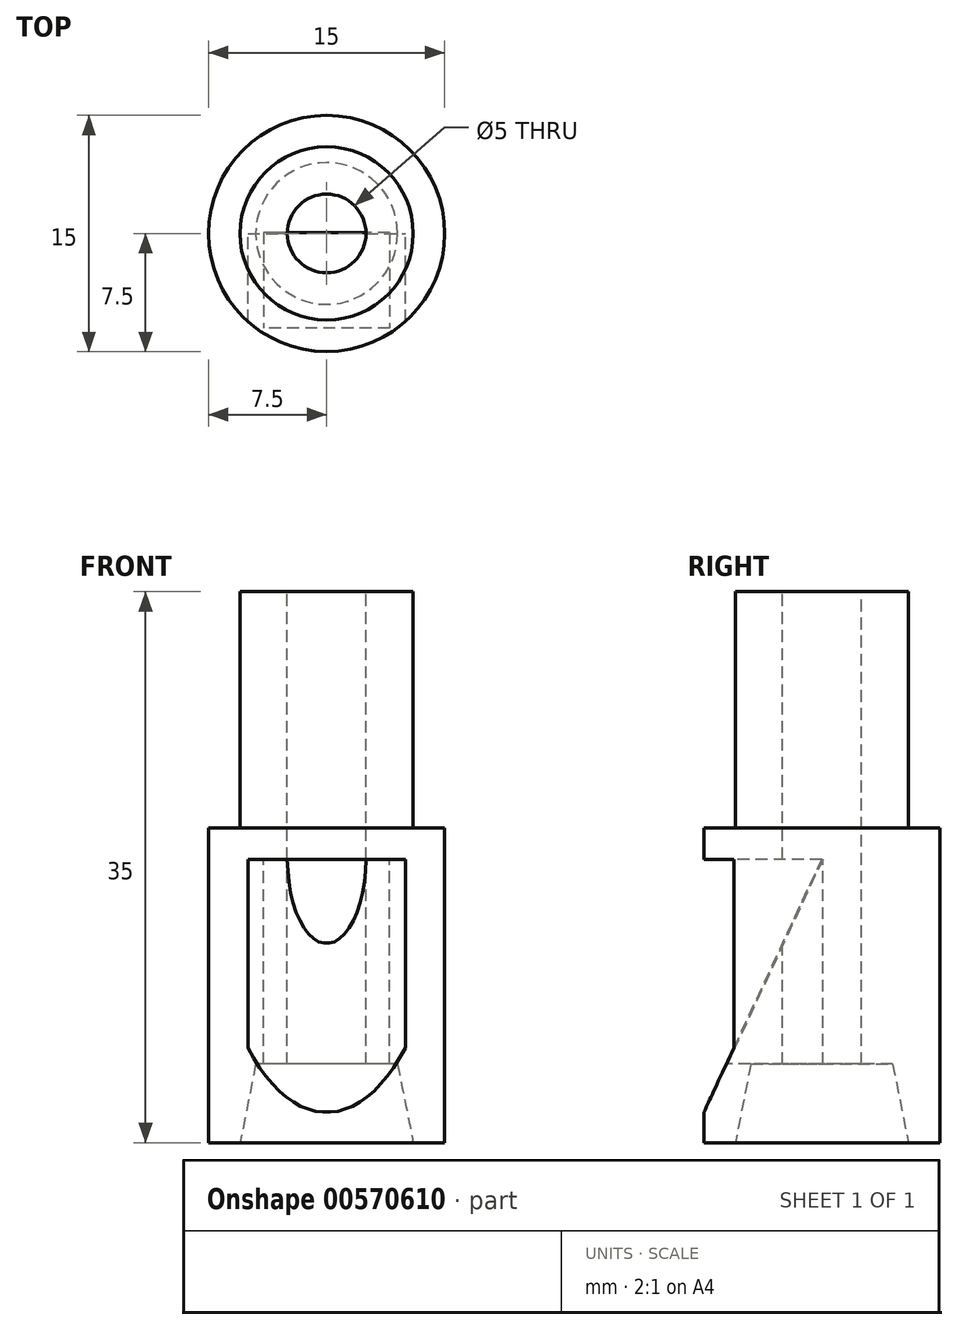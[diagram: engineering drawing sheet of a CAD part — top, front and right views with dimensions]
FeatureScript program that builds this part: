
annotation { "Feature Type Name" : "Feature", "Feature Type Description" : "" }
export const myFeature = defineFeature(function(context is Context, id is Id, definition is map)
    precondition{}
    {
        {
            var Q0;
            Q0=qCreatedBy(makeId("Front.planeOp"),FACE);
            var sketch = newSketch(context, id + "F0", { "sketchPlane" : qUnion([Q0])});
            skLineSegment(sketch, "E0", {"start": v(7.5, 0) * mm, "end": v(5.5, 0) * mm});
            skLineSegment(sketch, "E1", {"start": v(5.5, 0) * mm, "end": v(4.5, 5) * mm});
            skLineSegment(sketch, "E2", {"start": v(4.5, 5) * mm, "end": v(2.5, 5) * mm});
            skLineSegment(sketch, "E3", {"start": v(2.5, 5) * mm, "end": v(2.5, 35) * mm});
            skLineSegment(sketch, "E4", {"start": v(2.5, 35) * mm, "end": v(5.5, 35) * mm});
            skLineSegment(sketch, "E5", {"start": v(5.5, 35) * mm, "end": v(5.5, 20) * mm});
            skLineSegment(sketch, "E6", {"start": v(5.5, 20) * mm, "end": v(7.5, 20) * mm});
            skLineSegment(sketch, "E7", {"start": v(7.5, 20) * mm, "end": v(7.5, 0) * mm});
            skLineSegment(sketch, "E8", {"start": v(0, 13.32) * mm, "end": v(0, 5.67) * mm});
            skSolve(sketch);
        }
        {
            var Q0;
            Q0=makeQuery(id+"F0.imprint","IMPRINT",FACE,{"disambiguationData":[TD([[makeQuery(id+"F0.imprint","IMPRINT",EDGE,{"derivedFrom":sQuery(id+"F0.wireOp",EDGE,"E0")}),-1.0]])]});
            var Q1;
            Q1=sQuery(id+"F0.wireOp",EDGE,"E8");
            revolve(context, id + "F1", {"entities" : qUnion([Q0]), "axis" : qUnion([Q1]), "revolveType" : RevolveType.FULL});
        }
        {
            var Q0;
            Q0=qCreatedBy(makeId("Right.planeOp"),FACE);
            var sketch = newSketch(context, id + "F2", { "sketchPlane" : qUnion([Q0])});
            skLineSegment(sketch, "E9", {"start": v(-10.7, -4.93) * mm, "end": v(0, 18) * mm});
            skLineSegment(sketch, "E10", {"start": v(0, 18) * mm, "end": v(-10.7, 18) * mm});
            skLineSegment(sketch, "E11", {"start": v(-10.7, 18) * mm, "end": v(-10.7, -4.93) * mm});
            skSolve(sketch);
        }
        {
            var Q0;
            Q0=makeQuery(id+"F2.imprint","IMPRINT",FACE,{"disambiguationData":[TD([[makeQuery(id+"F2.imprint","IMPRINT",EDGE,{"derivedFrom":sQuery(id+"F2.wireOp",EDGE,"E9")}),1.0]])]});
            extrude(context, id + "F3", {"entities" : qUnion([Q0]), "operationType" : NewBodyOperationType.REMOVE, "endBound" : BoundingType.SYMMETRIC, "oppositeDirection" : true, "depth" : 10 * mm, "offsetDistance" : 25 * mm});
        }
        {
            var Q0;
            Q0=qCreatedBy(makeId("Right.planeOp"),FACE);
            var sketch = newSketch(context, id + "F4", { "sketchPlane" : qUnion([Q0])});
            skLineSegment(sketch, "E12", {"start": v(0.06, 5) * mm, "end": v(-6, 5) * mm});
            skLineSegment(sketch, "E13", {"start": v(0.06, 5) * mm, "end": v(0.06, 18) * mm});
            skLineSegment(sketch, "E14", {"start": v(0.06, 18) * mm, "end": v(-6, 5) * mm});
            skSolve(sketch);
        }
        {
            var Q0;
            Q0=makeQuery(id+"F4.imprint","IMPRINT",FACE,{"disambiguationData":[TD([[makeQuery(id+"F4.imprint","IMPRINT",EDGE,{"derivedFrom":sQuery(id+"F4.wireOp",EDGE,"E12")}),-1.0]])]});
            extrude(context, id + "F5", {"entities" : qUnion([Q0]), "endBound" : BoundingType.SYMMETRIC, "depth" : 8 * mm, "offsetDistance" : 25 * mm});
        }
    });
